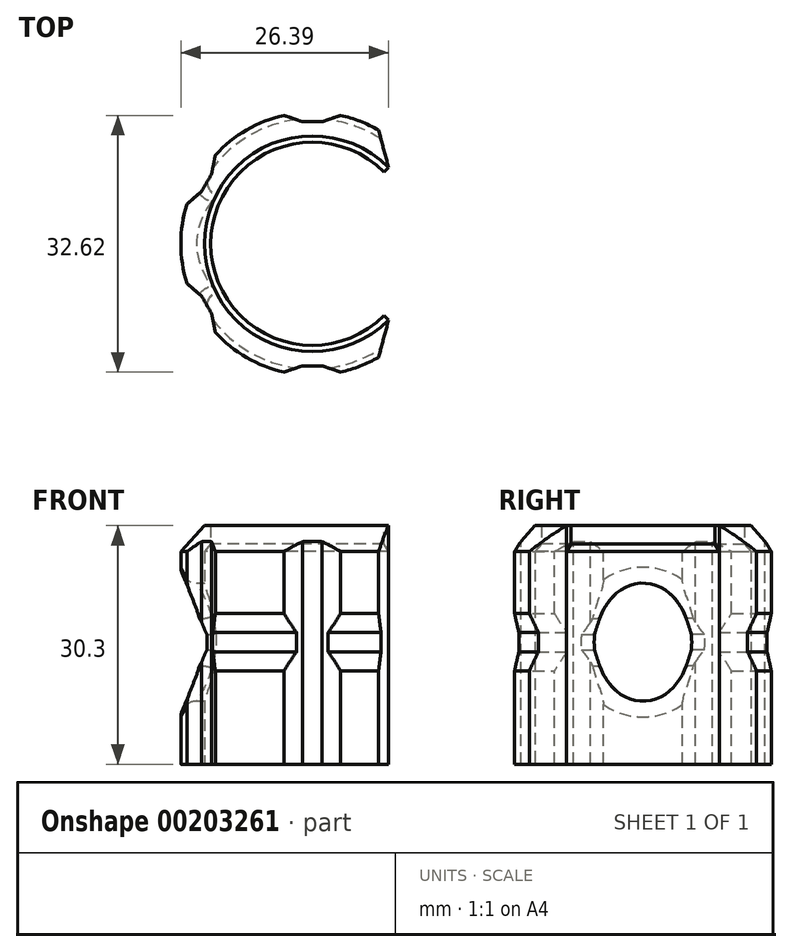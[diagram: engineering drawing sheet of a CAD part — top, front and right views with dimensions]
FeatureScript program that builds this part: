
annotation { "Feature Type Name" : "Feature", "Feature Type Description" : "" }
export const myFeature = defineFeature(function(context is Context, id is Id, definition is map)
    precondition{}
    {
        {
            var Q0;
            Q0=qCreatedBy(makeId("Front.planeOp"),FACE);
            var sketch = newSketch(context, id + "F0", { "sketchPlane" : qUnion([Q0])});
            skLineSegment(sketch, "E0", {"start": v(-13.7, 0) * mm, "end": v(-13.7, 27) * mm});
            skLineSegment(sketch, "E1", {"start": v(-13.7, 27) * mm, "end": v(-12.9, 28) * mm});
            skLineSegment(sketch, "E2", {"start": v(-12.9, 28) * mm, "end": v(-12.9, 30.3) * mm});
            skLineSegment(sketch, "E3", {"start": v(-12.9, 30.3) * mm, "end": v(-13.7, 30.3) * mm});
            skLineSegment(sketch, "E4", {"start": v(-16.7, 27) * mm, "end": v(-16.7, 19.15) * mm});
            skLineSegment(sketch, "E5", {"start": v(-16.7, 0) * mm, "end": v(-13.7, 0) * mm});
            skLineSegment(sketch, "E6", {"start": v(0, 0) * mm, "end": v(0, 30.3) * mm, "construction": true});
            skLineSegment(sketch, "E7", {"start": v(-16.7, 19.15) * mm, "end": v(-15.9, 16.75) * mm});
            skLineSegment(sketch, "E8", {"start": v(-15.9, 16.75) * mm, "end": v(-15.9, 14.25) * mm});
            skLineSegment(sketch, "E9", {"start": v(-15.9, 14.25) * mm, "end": v(-16.7, 11.85) * mm});
            skLineSegment(sketch, "E10", {"start": v(-15.9, 15.5) * mm, "end": v(-16.7, 15.5) * mm, "construction": true});
            skLineSegment(sketch, "E11.trimOffspring", {"start": v(-16.7, 11.85) * mm, "end": v(-16.7, 0) * mm});
            skLineSegment(sketch, "E12", {"start": v(-16.7, 27) * mm, "end": v(-13.7, 30.3) * mm});
            skSolve(sketch);
        }
        {
            var Q0;
            Q0=makeQuery(id+"F0.imprint","IMPRINT",FACE,{"disambiguationData":[TD([[makeQuery(id+"F0.imprint","IMPRINT",EDGE,{"derivedFrom":sQuery(id+"F0.wireOp",EDGE,"E0")}),1.0]])]});
            var Q1;
            Q1=sQuery(id+"F0.wireOp",EDGE,"E6");
            revolve(context, id + "F1", {"entities" : qUnion([Q0]), "axis" : qUnion([Q1]), "revolveType" : RevolveType.SYMMETRIC, "angle" : 270 * degree});
        }
        {
            var Q0;
            Q0=qCreatedBy(makeId("Right.planeOp"),FACE);
            var sketch = newSketch(context, id + "F2", { "sketchPlane" : qUnion([Q0])});
            skEllipse(sketch, "E13", {"center": v(0, 15.5) * mm, "majorRadius": 7.5 * mm, "minorRadius": 6 * mm, "majorAxis": v(0, -1)});
            skSolve(sketch);
        }
        {
            var Q0;
            Q0 = qSketchRegion(id + "F2", true);
            extrude(context, id + "F3", {"entities" : qUnion([Q0]), "operationType" : NewBodyOperationType.REMOVE, "endBound" : BoundingType.THROUGH_ALL, "oppositeDirection" : true, "depth" : 25 * mm});
        }
        {
            var Q0;
            Q0=makeQuery(id+"F3.boolean.opBoolean","INTERSECT",EDGE,{"derivedFrom":[makeQuery(id+"F1.opRevolve","SWEPT_FACE",FACE,{"disambiguationData":[OSD([sQuery(id+"F0.wireOp",EDGE,"E4")])]}),makeQuery(id+"F3.opExtrude","SWEPT_FACE",FACE,{"disambiguationData":[OSD([sQuery(id+"F2.wireOp",EDGE,"E13")])]})]});
            var Q1;
            Q1=makeQuery(id+"F3.boolean.opBoolean","INTERSECT",EDGE,{"disambiguationData":[OD(0.0)],"derivedFrom":[makeQuery(id+"F1.opRevolve","SWEPT_FACE",FACE,{"disambiguationData":[OSD([sQuery(id+"F0.wireOp",EDGE,"E7")])]}),makeQuery(id+"F3.opExtrude","SWEPT_FACE",FACE,{"disambiguationData":[OSD([sQuery(id+"F2.wireOp",EDGE,"E13")])]})]});
            var Q2;
            Q2=makeQuery(id+"F3.boolean.opBoolean","INTERSECT",EDGE,{"disambiguationData":[OD(0.0)],"derivedFrom":[makeQuery(id+"F1.opRevolve","SWEPT_FACE",FACE,{"disambiguationData":[OSD([sQuery(id+"F0.wireOp",EDGE,"E8")])]}),makeQuery(id+"F3.opExtrude","SWEPT_FACE",FACE,{"disambiguationData":[OSD([sQuery(id+"F2.wireOp",EDGE,"E13")])]})]});
            var Q3;
            Q3=makeQuery(id+"F3.boolean.opBoolean","INTERSECT",EDGE,{"disambiguationData":[OD(0.0)],"derivedFrom":[makeQuery(id+"F1.opRevolve","SWEPT_FACE",FACE,{"disambiguationData":[OSD([sQuery(id+"F0.wireOp",EDGE,"E9")])]}),makeQuery(id+"F3.opExtrude","SWEPT_FACE",FACE,{"disambiguationData":[OSD([sQuery(id+"F2.wireOp",EDGE,"E13")])]})]});
            var Q4;
            Q4=makeQuery(id+"F3.boolean.opBoolean","INTERSECT",EDGE,{"derivedFrom":[makeQuery(id+"F1.opRevolve","SWEPT_FACE",FACE,{"disambiguationData":[OSD([sQuery(id+"F0.wireOp",EDGE,"E11.trimOffspring")])]}),makeQuery(id+"F3.opExtrude","SWEPT_FACE",FACE,{"disambiguationData":[OSD([sQuery(id+"F2.wireOp",EDGE,"E13")])]})]});
            var Q5;
            Q5=makeQuery(id+"F3.boolean.opBoolean","INTERSECT",EDGE,{"disambiguationData":[OD(1.0)],"derivedFrom":[makeQuery(id+"F1.opRevolve","SWEPT_FACE",FACE,{"disambiguationData":[OSD([sQuery(id+"F0.wireOp",EDGE,"E9")])]}),makeQuery(id+"F3.opExtrude","SWEPT_FACE",FACE,{"disambiguationData":[OSD([sQuery(id+"F2.wireOp",EDGE,"E13")])]})]});
            var Q6;
            Q6=makeQuery(id+"F3.boolean.opBoolean","INTERSECT",EDGE,{"disambiguationData":[OD(1.0)],"derivedFrom":[makeQuery(id+"F1.opRevolve","SWEPT_FACE",FACE,{"disambiguationData":[OSD([sQuery(id+"F0.wireOp",EDGE,"E8")])]}),makeQuery(id+"F3.opExtrude","SWEPT_FACE",FACE,{"disambiguationData":[OSD([sQuery(id+"F2.wireOp",EDGE,"E13")])]})]});
            var Q7;
            Q7=makeQuery(id+"F3.boolean.opBoolean","INTERSECT",EDGE,{"disambiguationData":[OD(1.0)],"derivedFrom":[makeQuery(id+"F1.opRevolve","SWEPT_FACE",FACE,{"disambiguationData":[OSD([sQuery(id+"F0.wireOp",EDGE,"E7")])]}),makeQuery(id+"F3.opExtrude","SWEPT_FACE",FACE,{"disambiguationData":[OSD([sQuery(id+"F2.wireOp",EDGE,"E13")])]})]});
            fillet(context, id + "F4", {"entities" : qUnion([Q0, Q1, Q2, Q3, Q4, Q5, Q6, Q7]), "radius" : 2 * mm, "tangentPropagation" : true, "allowEdgeOverflow" : false});
        }
        {
            var Q0;
            Q0=makeQuery(id+"F1.opRevolve","SWEPT_FACE",FACE,{"disambiguationData":[OSD([sQuery(id+"F0.wireOp",EDGE,"E3")])]});
            var sketch = newSketch(context, id + "F5", { "sketchPlane" : qUnion([Q0])});
            skLineSegment(sketch, "E14", {"start": v(-3.6, 16.3) * mm, "end": v(-1.25, 15.5) * mm});
            skLineSegment(sketch, "E15", {"start": v(-1.25, 15.5) * mm, "end": v(1.25, 15.5) * mm});
            skLineSegment(sketch, "E16", {"start": v(1.25, 15.5) * mm, "end": v(3.6, 16.3) * mm});
            skLineSegment(sketch, "E17", {"start": v(0, 15.5) * mm, "end": v(0, 16.7) * mm, "construction": true});
            skLineSegment(sketch, "E18.1.0", {"start": v(-15.92, 5.04) * mm, "end": v(-14.05, 6.67) * mm});
            skLineSegment(sketch, "E18.1.1", {"start": v(-14.05, 6.67) * mm, "end": v(-12.8, 8.84) * mm});
            skLineSegment(sketch, "E18.1.2", {"start": v(-12.8, 8.84) * mm, "end": v(-12.32, 11.27) * mm});
            skLineSegment(sketch, "E18.2.0", {"start": v(-12.32, -11.27) * mm, "end": v(-12.8, -8.84) * mm});
            skLineSegment(sketch, "E18.2.1", {"start": v(-12.8, -8.84) * mm, "end": v(-14.05, -6.67) * mm});
            skLineSegment(sketch, "E18.2.2", {"start": v(-14.05, -6.67) * mm, "end": v(-15.92, -5.04) * mm});
            skPoint(sketch, "E18.center", {"position": v(0, 0) * mm});
            skLineSegment(sketch, "E18.anchor1", {"start": v(0, 0) * mm, "end": v(-3.6, 16.3) * mm, "construction": true});
            skLineSegment(sketch, "E18.anchor2", {"start": v(0, 0) * mm, "end": v(3.6, -16.3) * mm, "construction": true});
            skLineSegment(sketch, "E19.1.3.0", {"start": v(3.6, -16.3) * mm, "end": v(1.25, -15.5) * mm});
            skLineSegment(sketch, "E19.3.3.0", {"start": v(1.25, -15.5) * mm, "end": v(-1.25, -15.5) * mm});
            skLineSegment(sketch, "E19.6.3.0", {"start": v(-1.25, -15.5) * mm, "end": v(-3.6, -16.3) * mm});
            skArc(sketch, "E20.0", {"start": v(3.6, -16.3) * mm, "mid": v(0, -16.7) * mm, "end": v(-3.6, -16.3) * mm});
            skArc(sketch, "E21.trimOffspring", {"start": v(-15.92, 5.04) * mm, "mid": v(-14.46, 8.35) * mm, "end": v(-12.32, 11.27) * mm});
            skArc(sketch, "E22.trimOffspring", {"start": v(-3.6, 16.3) * mm, "mid": v(0, 16.7) * mm, "end": v(3.6, 16.3) * mm});
            skArc(sketch, "E23.trimOffspring", {"start": v(-12.32, -11.27) * mm, "mid": v(-14.46, -8.35) * mm, "end": v(-15.92, -5.04) * mm});
            skLineSegment(sketch, "E24", {"start": v(9.69, 9.69) * mm, "end": v(8.42, 14.42) * mm});
            skLineSegment(sketch, "E25", {"start": v(9.69, 9.69) * mm, "end": v(11.8, 11.8) * mm});
            skArc(sketch, "E26.trimOffspring", {"start": v(8.42, 14.42) * mm, "mid": v(10.2, 13.22) * mm, "end": v(11.8, 11.8) * mm});
            skPoint(sketch, "E27.orphan", {"position": v(11.8, -11.8) * mm});
            skLineSegment(sketch, "E28.MirrorCS", {"start": v(9.69, -9.69) * mm, "end": v(8.42, -14.42) * mm});
            skArc(sketch, "E29.MirrorCS", {"start": v(8.42, -14.42) * mm, "mid": v(10.2, -13.22) * mm, "end": v(11.8, -11.8) * mm});
            skLineSegment(sketch, "E30.MirrorCS", {"start": v(9.69, -9.69) * mm, "end": v(11.8, -11.8) * mm});
            skSolve(sketch);
        }
        {
            var Q0;
            Q0 = qSketchRegion(id + "F5", true);
            extrude(context, id + "F6", {"entities" : qUnion([Q0]), "operationType" : NewBodyOperationType.REMOVE, "endBound" : BoundingType.THROUGH_ALL, "oppositeDirection" : true, "depth" : 25 * mm});
        }
    });
